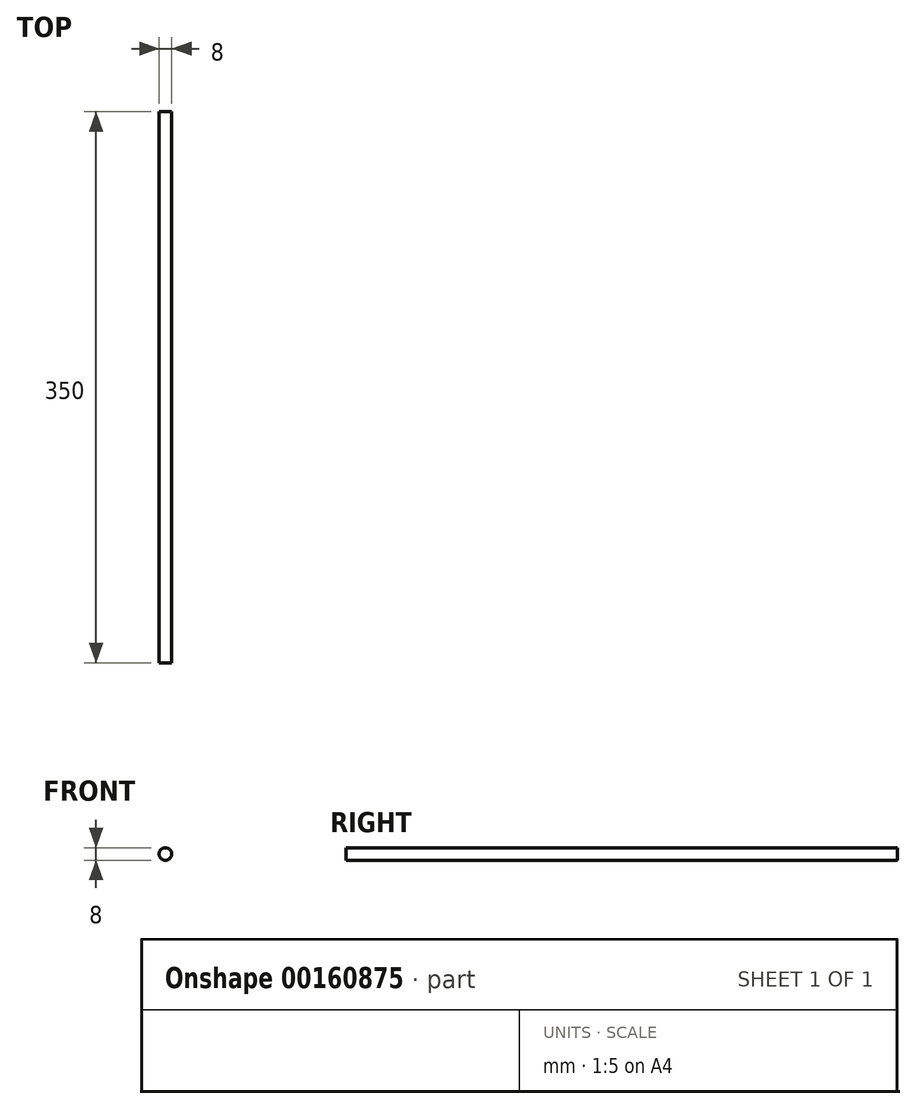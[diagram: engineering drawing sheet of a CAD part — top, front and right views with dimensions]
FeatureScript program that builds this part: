
annotation { "Feature Type Name" : "Feature", "Feature Type Description" : "" }
export const myFeature = defineFeature(function(context is Context, id is Id, definition is map)
    precondition{}
    {
        {
            var Q0;
            Q0=qCreatedBy(makeId("Front.planeOp"),FACE);
            var sketch = newSketch(context, id + "F0", { "sketchPlane" : qUnion([Q0])});
            skCircle(sketch, "E0", {"center": v(0, 0) * mm, "radius": 4 * mm});
            skSolve(sketch);
        }
        {
            var Q0;
            Q0 = qSketchRegion(id + "F0", true);
            extrude(context, id + "F1", {"entities" : qUnion([Q0]), "oppositeDirection" : true, "depth" : 350 * mm});
        }
    });
